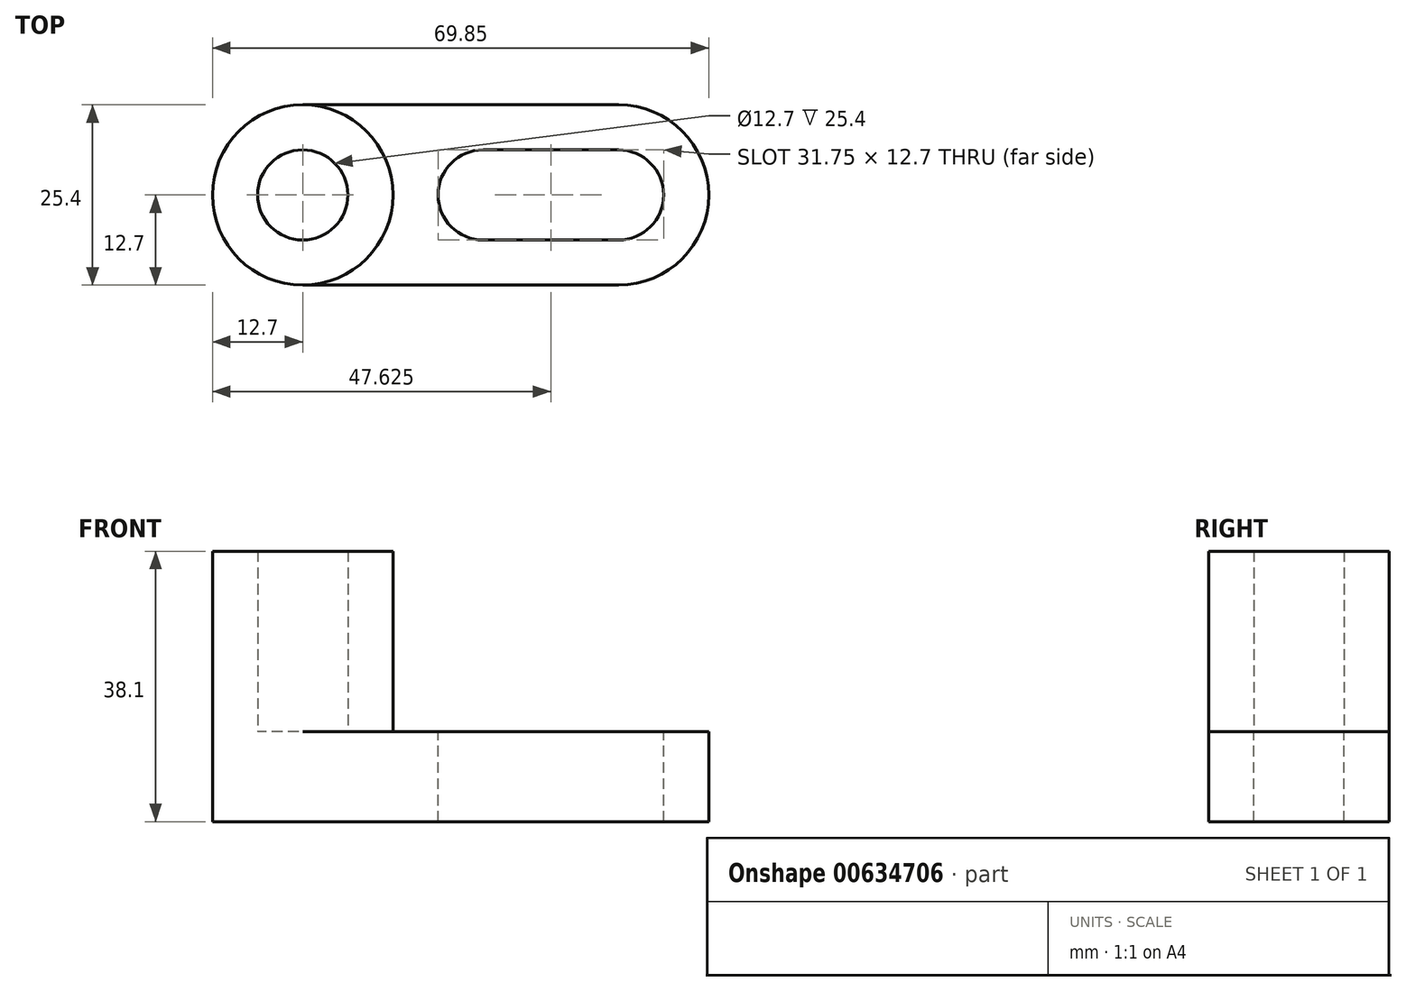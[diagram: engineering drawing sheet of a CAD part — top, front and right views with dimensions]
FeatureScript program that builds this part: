
annotation { "Feature Type Name" : "Feature", "Feature Type Description" : "" }
export const myFeature = defineFeature(function(context is Context, id is Id, definition is map)
    precondition{}
    {
        {
            var Q0;
            Q0=qCreatedBy(makeId("Front.planeOp"),FACE);
            var sketch = newSketch(context, id + "F0", { "sketchPlane" : qUnion([Q0])});
            skLineSegment(sketch, "E0", {"start": v(0, 0) * mm, "end": v(69.85, 0) * mm});
            skLineSegment(sketch, "E1", {"start": v(69.85, 0) * mm, "end": v(69.85, 12.7) * mm});
            skLineSegment(sketch, "E2", {"start": v(69.85, 12.7) * mm, "end": v(0, 12.7) * mm});
            skLineSegment(sketch, "E3", {"start": v(0, 12.7) * mm, "end": v(0, 0) * mm});
            skSolve(sketch);
        }
        {
            var Q0;
            Q0=qSketchRegion(id+"F0",true);
            extrude(context, id + "F1", {"entities" : qUnion([Q0]), "depth" : 25.4 * mm, "offsetDistance" : 25.4 * mm});
        }
        {
            var Q0;
            Q0=makeQuery(id+"F1.opExtrude","SWEPT_FACE",FACE,{"disambiguationData":[OSD([sQuery(id+"F0.wireOp",EDGE,"E2")])]});
            var sketch = newSketch(context, id + "F2", { "sketchPlane" : qUnion([Q0])});
            skCircle(sketch, "E4", {"center": v(12.7, -12.7) * mm, "radius": 6.35 * mm});
            skCircle(sketch, "E5", {"center": v(12.7, -12.7) * mm, "radius": 12.7 * mm});
            skSolve(sketch);
        }
        {
            var Q0;
            Q0=qSketchRegion(id+"F2",true);
            extrude(context, id + "F3", {"entities" : qUnion([Q0]), "operationType" : NewBodyOperationType.ADD, "depth" : 25.4 * mm, "offsetDistance" : 25.4 * mm});
        }
        {
            var Q0;
            {var subQ0=sQuery(id+"F0.wireOp",EDGE,"E3");var subQ1=sQuery(id+"F0.wireOp",EDGE,"E2");var subQ2=makeQuery(id+"F1.opExtrude","SWEPT_FACE",FACE,{"disambiguationData":[OSD([subQ1])]});Q0=makeQuery(id+"F3.boolean.opBoolean","SPLIT",FACE,{"disambiguationData":[TD([makeQuery(id+"F1.opExtrude","CAP_FACE",FACE,{"disambiguationData":[OSD([sQuery(id+"F0.wireOp",EDGE,"E0"),sQuery(id+"F0.wireOp",EDGE,"E1"),subQ1,subQ0])],"isStart":false}),subQ2,makeQuery(id+"F1.opExtrude","SWEPT_FACE",FACE,{"disambiguationData":[OSD([subQ0])]}),makeQuery(id+"F3.opExtrude","SWEPT_FACE",FACE,{"disambiguationData":[OSD([sQuery(id+"F2.wireOp",EDGE,"E5")])]})])],"derivedFrom":subQ2});}
            var Q1;
            {var subQ0=sQuery(id+"F0.wireOp",EDGE,"E3");var subQ1=sQuery(id+"F0.wireOp",EDGE,"E2");var subQ2=makeQuery(id+"F1.opExtrude","SWEPT_FACE",FACE,{"disambiguationData":[OSD([subQ1])]});Q1=makeQuery(id+"F3.boolean.opBoolean","SPLIT",FACE,{"disambiguationData":[TD([makeQuery(id+"F1.opExtrude","CAP_FACE",FACE,{"disambiguationData":[OSD([sQuery(id+"F0.wireOp",EDGE,"E0"),sQuery(id+"F0.wireOp",EDGE,"E1"),subQ1,subQ0])],"isStart":true}),subQ2,makeQuery(id+"F1.opExtrude","SWEPT_FACE",FACE,{"disambiguationData":[OSD([subQ0])]}),makeQuery(id+"F3.opExtrude","SWEPT_FACE",FACE,{"disambiguationData":[OSD([sQuery(id+"F2.wireOp",EDGE,"E5")])]})])],"derivedFrom":subQ2});}
            extrude(context, id + "F4", {"entities" : qUnion([Q0, Q1]), "operationType" : NewBodyOperationType.REMOVE, "oppositeDirection" : true, "depth" : 25.4 * mm, "offsetDistance" : 25.4 * mm});
        }
        {
            var Q0;
            {var subQ0=sQuery(id+"F0.wireOp",EDGE,"E2");var subQ1=makeQuery(id+"F1.opExtrude","SWEPT_FACE",FACE,{"disambiguationData":[OSD([subQ0])]});var subQ2=sQuery(id+"F0.wireOp",EDGE,"E1");var subQ3=sQuery(id+"F0.wireOp",EDGE,"E3");var subQ4=sQuery(id+"F0.wireOp",EDGE,"E0");Q0=makeQuery(id+"F3.boolean.opBoolean","SPLIT",FACE,{"disambiguationData":[TD([makeQuery(id+"F1.opExtrude","CAP_FACE",FACE,{"disambiguationData":[OSD([subQ4,subQ2,subQ0,subQ3])],"isStart":true}),makeQuery(id+"F1.opExtrude","CAP_FACE",FACE,{"disambiguationData":[OSD([subQ4,subQ2,subQ0,subQ3])],"isStart":false}),makeQuery(id+"F1.opExtrude","SWEPT_FACE",FACE,{"disambiguationData":[OSD([subQ2])]}),subQ1,makeQuery(id+"F3.opExtrude","SWEPT_FACE",FACE,{"disambiguationData":[OSD([sQuery(id+"F2.wireOp",EDGE,"E5")])]})])],"derivedFrom":subQ1});}
            var sketch = newSketch(context, id + "F5", { "sketchPlane" : qUnion([Q0])});
            skCircle(sketch, "E6", {"center": v(38.1, -12.7) * mm, "radius": 6.35 * mm});
            skCircle(sketch, "E7", {"center": v(57.15, -12.7) * mm, "radius": 6.35 * mm});
            skLineSegment(sketch, "E8", {"start": v(38.1, -6.35) * mm, "end": v(57.15, -6.35) * mm});
            skLineSegment(sketch, "E9", {"start": v(57.15, -19.05) * mm, "end": v(38.1, -19.05) * mm});
            skArc(sketch, "E10", {"start": v(57.15, -25.4) * mm, "mid": v(69.85, -12.7) * mm, "end": v(57.15, 0) * mm});
            skSolve(sketch);
        }
        {
            var Q0;
            {var subQ0=sQuery(id+"F5.wireOp",EDGE,"E6");var subQ1=makeQuery(id+"F5.imprint","INTERSECT",VERTEX,{"derivedFrom":[subQ0,sQuery(id+"F5.wireOp",EDGE,"E8")]});Q0=makeQuery(id+"F5.imprint","IMPRINT",FACE,{"disambiguationData":[TD([[makeQuery(id+"F5.imprint","IMPRINT",EDGE,{"disambiguationData":[TD([[subQ1,-1.0]])],"derivedFrom":subQ0}),1.0]])]});}
            var Q1;
            {var subQ0=sQuery(id+"F5.wireOp",EDGE,"E8");Q1=makeQuery(id+"F5.imprint","IMPRINT",FACE,{"disambiguationData":[TD([[makeQuery(id+"F5.imprint","IMPRINT",EDGE,{"derivedFrom":subQ0}),-1.0]])]});}
            var Q2;
            {var subQ0=sQuery(id+"F5.wireOp",EDGE,"E7");var subQ1=makeQuery(id+"F5.imprint","INTERSECT",VERTEX,{"derivedFrom":[subQ0,sQuery(id+"F5.wireOp",EDGE,"E8")]});Q2=makeQuery(id+"F5.imprint","IMPRINT",FACE,{"disambiguationData":[TD([[makeQuery(id+"F5.imprint","IMPRINT",EDGE,{"disambiguationData":[TD([[subQ1,-1.0]])],"derivedFrom":subQ0}),1.0]])]});}
            var Q3;
            {var subQ0=sQuery(id+"F5.wireOp",EDGE,"E10");var subQ1=sQuery(id+"F0.wireOp",EDGE,"E2");var subQ2=sQuery(id+"F0.wireOp",EDGE,"E1");var subQ5=makeQuery(id+"F1.opExtrude","SWEPT_EDGE",EDGE,{"disambiguationData":[OSD([subQ2,subQ1])]});var subQ6=makeQuery(id+"F5.imprint","INTERSECT",VERTEX,{"derivedFrom":[subQ5,subQ0]});Q3=makeQuery(id+"F5.imprint","IMPRINT",FACE,{"disambiguationData":[TD([[makeQuery(id+"F5.imprint","IMPRINT",EDGE,{"disambiguationData":[TD([[subQ6,-1.0]])],"derivedFrom":subQ0}),-1.0]])]});}
            var Q4;
            {var subQ0=sQuery(id+"F5.wireOp",EDGE,"E10");var subQ1=sQuery(id+"F0.wireOp",EDGE,"E2");var subQ2=sQuery(id+"F0.wireOp",EDGE,"E1");var subQ5=makeQuery(id+"F1.opExtrude","SWEPT_EDGE",EDGE,{"disambiguationData":[OSD([subQ2,subQ1])]});var subQ6=makeQuery(id+"F5.imprint","INTERSECT",VERTEX,{"derivedFrom":[subQ5,subQ0]});Q4=makeQuery(id+"F5.imprint","IMPRINT",FACE,{"disambiguationData":[TD([[makeQuery(id+"F5.imprint","IMPRINT",EDGE,{"disambiguationData":[TD([[subQ6,1.0]])],"derivedFrom":subQ0}),-1.0]])]});}
            extrude(context, id + "F6", {"entities" : qUnion([Q0, Q1, Q2, Q3, Q4]), "operationType" : NewBodyOperationType.REMOVE, "oppositeDirection" : true, "depth" : 25.4 * mm, "offsetDistance" : 25.4 * mm});
        }
    });
